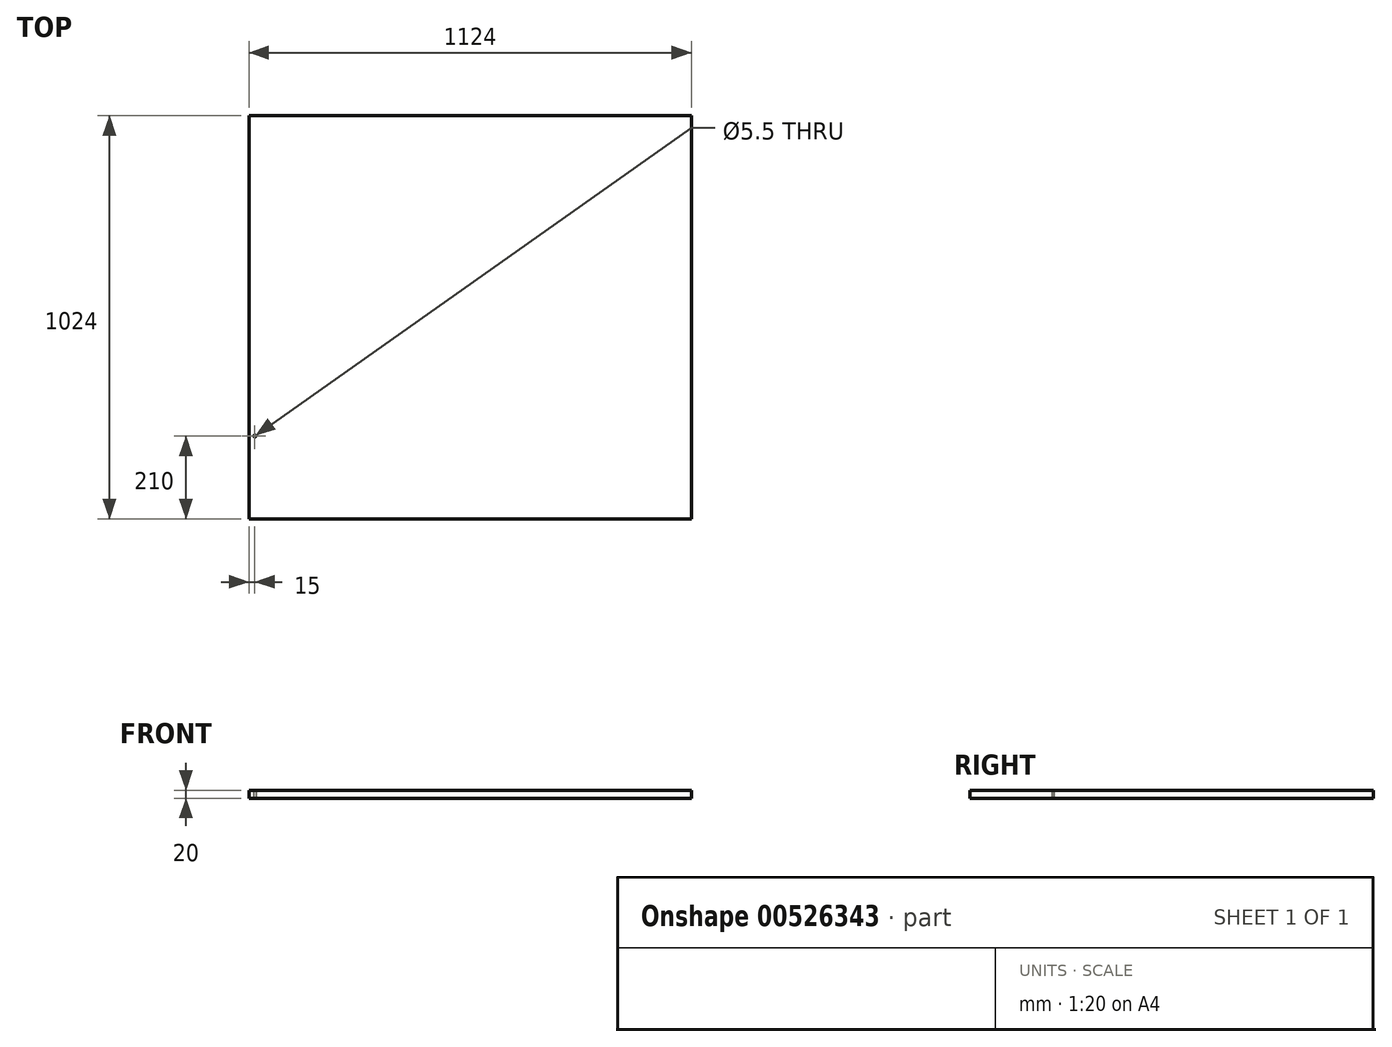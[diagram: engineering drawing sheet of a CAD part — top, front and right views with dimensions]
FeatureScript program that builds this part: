
annotation { "Feature Type Name" : "Feature", "Feature Type Description" : "" }
export const myFeature = defineFeature(function(context is Context, id is Id, definition is map)
    precondition{}
    {
        {
            var Q0;
            Q0=qCreatedBy(makeId("Top.planeOp"),FACE);
            var sketch = newSketch(context, id + "F0", { "sketchPlane" : qUnion([Q0])});
            skLineSegment(sketch, "E0.bottom", {"start": v(562, 512) * mm, "end": v(-562, 512) * mm});
            skLineSegment(sketch, "E0.top", {"start": v(562, -512) * mm, "end": v(-562, -512) * mm});
            skLineSegment(sketch, "E0.left", {"start": v(562, 512) * mm, "end": v(562, -512) * mm});
            skLineSegment(sketch, "E0.right", {"start": v(-562, 512) * mm, "end": v(-562, -512) * mm});
            skPoint(sketch, "E0.middle", {"position": v(0, 0) * mm});
            skPoint(sketch, "E1", {"position": v(-547, -302) * mm});
            skSolve(sketch);
        }
        {
            var Q0;
            Q0=makeQuery(id+"F0.imprint","IMPRINT",FACE,{"disambiguationData":[TD([[makeQuery(id+"F0.imprint","IMPRINT",EDGE,{"derivedFrom":sQuery(id+"F0.wireOp",EDGE,"E0.bottom")}),1.0]])]});
            extrude(context, id + "F1", {"entities" : qUnion([Q0]), "depth" : 20 * mm, "offsetDistance" : 25 * mm});
        }
        {
            var Q0;
            Q0=sQuery(id+"F0.wireOp",VERTEX,"E1");
            var Q1;
            Q1=makeQuery(id+"F1.opExtrude","SWEPT_BODY",BODY,{"disambiguationData":[OSD([sQuery(id+"F0.wireOp",EDGE,"E0.bottom"),sQuery(id+"F0.wireOp",EDGE,"E0.top"),sQuery(id+"F0.wireOp",EDGE,"E0.left"),sQuery(id+"F0.wireOp",EDGE,"E0.right")])]});
            hole(context, id + "F2", {"style" : HoleStyle.SIMPLE, "endStyle" : HoleEndStyle.THROUGH, "oppositeDirection" : true, "standardTappedOrClearance" : lookupTablePath({ "standard" : "ISO", "fit" : "Normal", "size" : "M5", "type" : "Clearance" }), "standardBlindInLast" : lookupTablePath({ "fit" : "Standard", "standard" : "ISO", "size" : "M5", "type" : "Clearance" }), "holeDiameter" : 5.5 * mm, "isTappedThrough" : true, "tappedDepth" : 12 * mm, "tapClearance" : 3, "locations" : qUnion([Q0]), "scope" : qUnion([Q1])});
        }
    });
